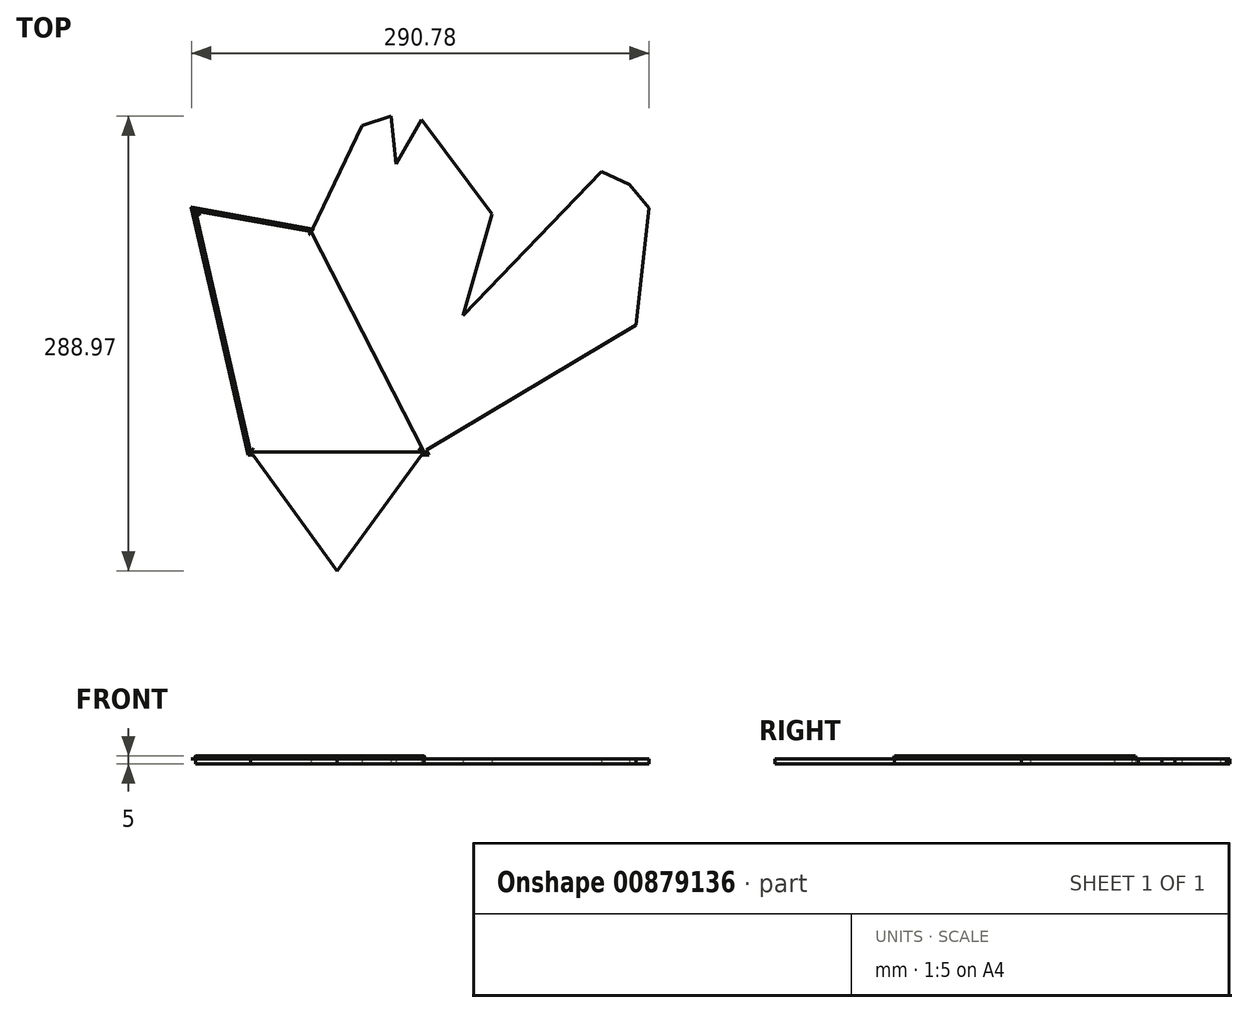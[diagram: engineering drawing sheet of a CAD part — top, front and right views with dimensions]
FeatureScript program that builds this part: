
annotation { "Feature Type Name" : "Feature", "Feature Type Description" : "" }
export const myFeature = defineFeature(function(context is Context, id is Id, definition is map)
    precondition{}
    {
        {
            var Q0;
            Q0=qCreatedBy(makeId("Top.planeOp"),FACE);
            var sketch = newSketch(context, id + "F0", { "sketchPlane" : qUnion([Q0])});
            skLineSegment(sketch, "E0", {"start": v(-120.67, -109.95) * mm, "end": v(-10.67, -109.95) * mm});
            skLineSegment(sketch, "E1", {"start": v(-120.67, -109.95) * mm, "end": v(-140.78, -22.23) * mm});
            skLineSegment(sketch, "E2", {"start": v(-140.78, -22.23) * mm, "end": v(-10.67, -109.95) * mm});
            skLineSegment(sketch, "E3", {"start": v(-10.67, -109.95) * mm, "end": v(-51.68, -29.84) * mm});
            skLineSegment(sketch, "E4", {"start": v(-51.68, -29.84) * mm, "end": v(-140.78, -22.23) * mm});
            skLineSegment(sketch, "E5", {"start": v(-140.78, -22.23) * mm, "end": v(-155.75, 43.08) * mm});
            skLineSegment(sketch, "E6", {"start": v(-155.75, 43.08) * mm, "end": v(-51.68, -29.84) * mm});
            skLineSegment(sketch, "E7", {"start": v(-51.68, -29.84) * mm, "end": v(-82.21, 29.8) * mm});
            skLineSegment(sketch, "E8", {"start": v(-82.21, 29.8) * mm, "end": v(-155.75, 43.08) * mm});
            skLineSegment(sketch, "E9.4.1", {"start": v(-10.67, -109.95) * mm, "end": v(66.55, -63.72) * mm});
            skLineSegment(sketch, "E9.4.7", {"start": v(66.55, -63.72) * mm, "end": v(124.03, -29.3) * mm});
            skPoint(sketch, "E9.center", {"position": v(-65.67, -185.66) * mm});
            skLineSegment(sketch, "E10", {"start": v(-51.68, -29.84) * mm, "end": v(-23.12, 17.9) * mm});
            skLineSegment(sketch, "E11", {"start": v(-82.21, 29.8) * mm, "end": v(-50, 97.22) * mm});
            skLineSegment(sketch, "E12.MirrorCS", {"start": v(-28.45, 72.7) * mm, "end": v(-50, 97.22) * mm});
            skLineSegment(sketch, "E13", {"start": v(-28.45, 72.7) * mm, "end": v(-31.43, 103.3) * mm});
            skLineSegment(sketch, "E14", {"start": v(-31.43, 103.3) * mm, "end": v(-50, 97.22) * mm});
            skLineSegment(sketch, "E15", {"start": v(-28.45, 72.7) * mm, "end": v(-10.67, -109.95) * mm});
            skLineSegment(sketch, "E16.MirrorCS", {"start": v(-31.43, 103.3) * mm, "end": v(-12.04, 100.91) * mm});
            skLineSegment(sketch, "E17.MirrorCS", {"start": v(-28.45, 72.7) * mm, "end": v(-12.04, 100.91) * mm});
            skLineSegment(sketch, "E18.MirrorCS", {"start": v(32.58, 40.97) * mm, "end": v(-12.04, 100.91) * mm});
            skLineSegment(sketch, "E19.MirrorCS", {"start": v(14.12, -23.44) * mm, "end": v(32.58, 40.97) * mm});
            skLineSegment(sketch, "E20.MirrorCS", {"start": v(14.12, -23.44) * mm, "end": v(-23.12, 17.9) * mm});
            skLineSegment(sketch, "E21.MirrorCS", {"start": v(-10.67, -109.95) * mm, "end": v(14.12, -23.44) * mm});
            skLineSegment(sketch, "E22.MirrorCS", {"start": v(119.89, 59.95) * mm, "end": v(132.41, 44.95) * mm});
            skLineSegment(sketch, "E23.MirrorCS", {"start": v(119.89, 59.95) * mm, "end": v(102.17, 68.19) * mm});
            skLineSegment(sketch, "E24.MirrorCS", {"start": v(101.15, 35.56) * mm, "end": v(119.89, 59.95) * mm});
            skLineSegment(sketch, "E25.MirrorCS", {"start": v(101.15, 35.56) * mm, "end": v(102.17, 68.19) * mm});
            skLineSegment(sketch, "E26.MirrorCS", {"start": v(101.15, 35.56) * mm, "end": v(132.41, 44.95) * mm});
            skLineSegment(sketch, "E27.MirrorCS", {"start": v(66.55, -63.72) * mm, "end": v(67.6, -8.1) * mm});
            skLineSegment(sketch, "E28.MirrorCS", {"start": v(32.58, 40.97) * mm, "end": v(102.17, 68.19) * mm});
            skLineSegment(sketch, "E29.MirrorCS", {"start": v(14.12, -23.44) * mm, "end": v(67.6, -8.1) * mm});
            skLineSegment(sketch, "E30.MirrorCS", {"start": v(101.15, 35.56) * mm, "end": v(-10.67, -109.95) * mm});
            skLineSegment(sketch, "E31.MirrorCS", {"start": v(124.03, -29.3) * mm, "end": v(132.41, 44.95) * mm});
            skLineSegment(sketch, "E32", {"start": v(-51.68, -29.84) * mm, "end": v(-50, 97.22) * mm});
            skLineSegment(sketch, "E33", {"start": v(-51.68, -29.84) * mm, "end": v(-28.45, 72.7) * mm});
            skLineSegment(sketch, "E34", {"start": v(-28.45, 72.7) * mm, "end": v(14.12, -23.44) * mm});
            skLineSegment(sketch, "E35", {"start": v(14.12, -23.44) * mm, "end": v(-12.04, 100.91) * mm});
            skLineSegment(sketch, "E36", {"start": v(14.12, -23.44) * mm, "end": v(102.17, 68.19) * mm});
            skLineSegment(sketch, "E37", {"start": v(14.12, -23.44) * mm, "end": v(101.15, 35.56) * mm});
            skLineSegment(sketch, "E38", {"start": v(66.55, -63.72) * mm, "end": v(101.15, 35.56) * mm});
            skLineSegment(sketch, "E39", {"start": v(66.55, -63.72) * mm, "end": v(132.41, 44.95) * mm});
            skLineSegment(sketch, "E40", {"start": v(-65.67, -185.66) * mm, "end": v(-120.67, -109.95) * mm});
            skLineSegment(sketch, "E41", {"start": v(-65.67, -185.66) * mm, "end": v(-10.67, -109.95) * mm});
            skSolve(sketch);
        }
        {
            var Q0;
            Q0 = qSketchRegion(id + "F75ZbTaoLFMl4lC_0", true);
            var Q1;
            {var subQ0=sQuery(id+"F0.wireOp",EDGE,"E10");Q1=makeQuery(id+"F0.imprint","IMPRINT",FACE,{"disambiguationData":[TD([[makeQuery(id+"F0.imprint","IMPRINT",EDGE,{"derivedFrom":subQ0}),1.0]])]});}
            var Q2;
            Q2=makeQuery(id+"F0.imprint","IMPRINT",FACE,{"disambiguationData":[TD([[makeQuery(id+"F0.imprint","IMPRINT",EDGE,{"derivedFrom":sQuery(id+"F0.wireOp",EDGE,"E2")}),1.0]])]});
            var Q3;
            {var subQ0=sQuery(id+"F0.wireOp",EDGE,"E3");Q3=makeQuery(id+"F0.imprint","IMPRINT",FACE,{"disambiguationData":[TD([[makeQuery(id+"F0.imprint","IMPRINT",EDGE,{"derivedFrom":subQ0}),-1.0]])]});}
            var Q4;
            Q4=makeQuery(id+"F0.imprint","IMPRINT",FACE,{"disambiguationData":[TD([[makeQuery(id+"F0.imprint","IMPRINT",EDGE,{"derivedFrom":sQuery(id+"F0.wireOp",EDGE,"E0")}),-1.0]])]});
            var Q5;
            Q5=makeQuery(id+"F0.imprint","IMPRINT",FACE,{"disambiguationData":[TD([[makeQuery(id+"F0.imprint","IMPRINT",EDGE,{"derivedFrom":sQuery(id+"F0.wireOp",EDGE,"E9.4.7")}),1.0]])]});
            var Q6;
            Q6=makeQuery(id+"F0.imprint","IMPRINT",FACE,{"disambiguationData":[TD([[makeQuery(id+"F0.imprint","IMPRINT",EDGE,{"derivedFrom":sQuery(id+"F0.wireOp",EDGE,"E1")}),-1.0]])]});
            var Q7;
            Q7=makeQuery(id+"F0.imprint","IMPRINT",FACE,{"disambiguationData":[TD([[makeQuery(id+"F0.imprint","IMPRINT",EDGE,{"derivedFrom":sQuery(id+"F0.wireOp",EDGE,"E4")}),-1.0]])]});
            var Q8;
            Q8=makeQuery(id+"F0.imprint","IMPRINT",FACE,{"disambiguationData":[TD([[makeQuery(id+"F0.imprint","IMPRINT",EDGE,{"derivedFrom":sQuery(id+"F0.wireOp",EDGE,"E6")}),1.0]])]});
            var Q9;
            Q9=makeQuery(id+"F0.imprint","IMPRINT",FACE,{"disambiguationData":[TD([[makeQuery(id+"F0.imprint","IMPRINT",EDGE,{"derivedFrom":sQuery(id+"F0.wireOp",EDGE,"E7")}),-1.0]])]});
            var Q10;
            {var subQ0=sQuery(id+"F0.wireOp",EDGE,"E9.4.1");Q10=makeQuery(id+"F0.imprint","IMPRINT",FACE,{"disambiguationData":[TD([[makeQuery(id+"F0.imprint","IMPRINT",EDGE,{"derivedFrom":subQ0}),1.0]])]});}
            var Q11;
            Q11=makeQuery(id+"F0.imprint","IMPRINT",FACE,{"disambiguationData":[TD([[makeQuery(id+"F0.imprint","IMPRINT",EDGE,{"derivedFrom":sQuery(id+"F0.wireOp",EDGE,"E12.MirrorCS")}),-1.0]])]});
            var Q12;
            Q12=makeQuery(id+"F0.imprint","IMPRINT",FACE,{"disambiguationData":[TD([[makeQuery(id+"F0.imprint","IMPRINT",EDGE,{"derivedFrom":sQuery(id+"F0.wireOp",EDGE,"E13")}),-1.0]])]});
            var Q13;
            Q13=makeQuery(id+"F0.imprint","IMPRINT",FACE,{"disambiguationData":[TD([[makeQuery(id+"F0.imprint","IMPRINT",EDGE,{"derivedFrom":sQuery(id+"F0.wireOp",EDGE,"E18.MirrorCS")}),1.0]])]});
            var Q14;
            Q14=makeQuery(id+"F0.imprint","IMPRINT",FACE,{"disambiguationData":[TD([[makeQuery(id+"F0.imprint","IMPRINT",EDGE,{"derivedFrom":sQuery(id+"F0.wireOp",EDGE,"E22.MirrorCS")}),-1.0]])]});
            var Q15;
            Q15=makeQuery(id+"F0.imprint","IMPRINT",FACE,{"disambiguationData":[TD([[makeQuery(id+"F0.imprint","IMPRINT",EDGE,{"derivedFrom":sQuery(id+"F0.wireOp",EDGE,"E23.MirrorCS")}),1.0]])]});
            var Q16;
            Q16=makeQuery(id+"F0.imprint","IMPRINT",FACE,{"disambiguationData":[TD([[makeQuery(id+"F0.imprint","IMPRINT",EDGE,{"derivedFrom":sQuery(id+"F0.wireOp",EDGE,"E19.MirrorCS")}),-1.0]])]});
            var Q17;
            Q17=makeQuery(id+"F0.imprint","IMPRINT",FACE,{"disambiguationData":[TD([[makeQuery(id+"F0.imprint","IMPRINT",EDGE,{"derivedFrom":sQuery(id+"F0.wireOp",EDGE,"E12.MirrorCS")}),1.0]])]});
            var Q18;
            {var subQ0=sQuery(id+"F0.wireOp",EDGE,"E20.MirrorCS");Q18=makeQuery(id+"F0.imprint","IMPRINT",FACE,{"disambiguationData":[TD([[makeQuery(id+"F0.imprint","IMPRINT",EDGE,{"derivedFrom":subQ0}),-1.0]])]});}
            var Q19;
            {var subQ2=sQuery(id+"F0.wireOp",EDGE,"E20.MirrorCS");Q19=makeQuery(id+"F0.imprint","IMPRINT",FACE,{"disambiguationData":[TD([[makeQuery(id+"F0.imprint","IMPRINT",EDGE,{"derivedFrom":subQ2}),1.0]])]});}
            var Q20;
            Q20=makeQuery(id+"F0.imprint","IMPRINT",FACE,{"disambiguationData":[TD([[makeQuery(id+"F0.imprint","IMPRINT",EDGE,{"derivedFrom":sQuery(id+"F0.wireOp",EDGE,"E17.MirrorCS")}),-1.0]])]});
            var Q21;
            {var subQ0=sQuery(id+"F0.wireOp",EDGE,"E21.MirrorCS");Q21=makeQuery(id+"F0.imprint","IMPRINT",FACE,{"disambiguationData":[TD([[makeQuery(id+"F0.imprint","IMPRINT",EDGE,{"derivedFrom":subQ0}),-1.0]])]});}
            var Q22;
            Q22=makeQuery(id+"F0.imprint","IMPRINT",FACE,{"disambiguationData":[TD([[makeQuery(id+"F0.imprint","IMPRINT",EDGE,{"derivedFrom":sQuery(id+"F0.wireOp",EDGE,"E25.MirrorCS")}),1.0]])]});
            var Q23;
            Q23=makeQuery(id+"F0.imprint","IMPRINT",FACE,{"disambiguationData":[TD([[makeQuery(id+"F0.imprint","IMPRINT",EDGE,{"derivedFrom":sQuery(id+"F0.wireOp",EDGE,"E26.MirrorCS")}),-1.0]])]});
            var Q24;
            {var subQ0=sQuery(id+"F0.wireOp",EDGE,"E27.MirrorCS");Q24=makeQuery(id+"F0.imprint","IMPRINT",FACE,{"disambiguationData":[TD([[makeQuery(id+"F0.imprint","IMPRINT",EDGE,{"derivedFrom":subQ0}),-1.0]])]});}
            var Q25;
            {var subQ0=sQuery(id+"F0.wireOp",EDGE,"E29.MirrorCS");Q25=makeQuery(id+"F0.imprint","IMPRINT",FACE,{"disambiguationData":[TD([[makeQuery(id+"F0.imprint","IMPRINT",EDGE,{"derivedFrom":subQ0}),1.0]])]});}
            extrude(context, id + "F1", {"entities" : qUnion([Q0, Q1, Q2, Q3, Q4, Q5, Q6, Q7, Q8, Q9, Q10, Q11, Q12, Q13, Q14, Q15, Q16, Q17, Q18, Q19, Q20, Q21, Q22, Q23, Q24, Q25]), "depth" : 3 * mm, "offsetDistance" : 25 * mm});
        }
        {
            var Q0;
            Q0=makeQuery(id+"F1.opExtrude","CAP_FACE",FACE,{"disambiguationData":[OSD([sQuery(id+"F0.wireOp",EDGE,"E1"),sQuery(id+"F0.wireOp",EDGE,"E5"),sQuery(id+"F0.wireOp",EDGE,"E8"),sQuery(id+"F0.wireOp",EDGE,"E9.4.1"),sQuery(id+"F0.wireOp",EDGE,"E9.4.7"),sQuery(id+"F0.wireOp",EDGE,"E11"),sQuery(id+"F0.wireOp",EDGE,"E14"),sQuery(id+"F0.wireOp",EDGE,"E16.MirrorCS"),sQuery(id+"F0.wireOp",EDGE,"E18.MirrorCS"),sQuery(id+"F0.wireOp",EDGE,"E22.MirrorCS"),sQuery(id+"F0.wireOp",EDGE,"E23.MirrorCS"),sQuery(id+"F0.wireOp",EDGE,"E28.MirrorCS"),sQuery(id+"F0.wireOp",EDGE,"E31.MirrorCS"),sQuery(id+"F0.wireOp",EDGE,"E40"),sQuery(id+"F0.wireOp",EDGE,"E41")])],"isStart":false});
            var sketch = newSketch(context, id + "F2", { "sketchPlane" : qUnion([Q0])});
            skLineSegment(sketch, "E42", {"start": v(-120.67, -109.95) * mm, "end": v(-10.67, -109.95) * mm});
            skLineSegment(sketch, "E43", {"start": v(-120.67, -109.95) * mm, "end": v(-140.78, -22.23) * mm});
            skLineSegment(sketch, "E44", {"start": v(-140.78, -22.23) * mm, "end": v(-10.67, -109.95) * mm});
            skLineSegment(sketch, "E45", {"start": v(-10.67, -109.95) * mm, "end": v(-51.68, -29.84) * mm});
            skLineSegment(sketch, "E46", {"start": v(-51.68, -29.84) * mm, "end": v(-140.78, -22.23) * mm});
            skLineSegment(sketch, "E47", {"start": v(-140.78, -22.23) * mm, "end": v(-155.75, 43.08) * mm});
            skLineSegment(sketch, "E48", {"start": v(-155.75, 43.08) * mm, "end": v(-51.68, -29.84) * mm});
            skLineSegment(sketch, "E49", {"start": v(-51.68, -29.84) * mm, "end": v(-82.21, 29.8) * mm});
            skLineSegment(sketch, "E50", {"start": v(-82.21, 29.8) * mm, "end": v(-155.75, 43.08) * mm});
            skLineSegment(sketch, "E51.4.1", {"start": v(-10.67, -109.95) * mm, "end": v(66.55, -63.72) * mm});
            skLineSegment(sketch, "E51.4.7", {"start": v(66.55, -63.72) * mm, "end": v(124.03, -29.3) * mm});
            skPoint(sketch, "E51.center", {"position": v(-65.67, -185.66) * mm});
            skLineSegment(sketch, "E52", {"start": v(-51.68, -29.84) * mm, "end": v(-23.12, 17.9) * mm});
            skLineSegment(sketch, "E53", {"start": v(-82.21, 29.8) * mm, "end": v(-50, 97.22) * mm});
            skLineSegment(sketch, "E54.MirrorCS", {"start": v(-28.45, 72.7) * mm, "end": v(-50, 97.22) * mm});
            skLineSegment(sketch, "E55", {"start": v(-28.45, 72.7) * mm, "end": v(-31.43, 103.3) * mm});
            skLineSegment(sketch, "E56", {"start": v(-31.43, 103.3) * mm, "end": v(-50, 97.22) * mm});
            skLineSegment(sketch, "E57", {"start": v(-28.45, 72.7) * mm, "end": v(-10.67, -109.95) * mm});
            skLineSegment(sketch, "E58.MirrorCS", {"start": v(-31.43, 103.3) * mm, "end": v(-12.04, 100.91) * mm});
            skLineSegment(sketch, "E59.MirrorCS", {"start": v(-28.45, 72.7) * mm, "end": v(-12.04, 100.91) * mm});
            skLineSegment(sketch, "E60.MirrorCS", {"start": v(32.58, 40.97) * mm, "end": v(-12.04, 100.91) * mm});
            skLineSegment(sketch, "E61.MirrorCS", {"start": v(14.12, -23.44) * mm, "end": v(32.58, 40.97) * mm});
            skLineSegment(sketch, "E62.MirrorCS", {"start": v(14.12, -23.44) * mm, "end": v(-23.12, 17.9) * mm});
            skLineSegment(sketch, "E63.MirrorCS", {"start": v(-10.67, -109.95) * mm, "end": v(14.12, -23.44) * mm});
            skLineSegment(sketch, "E64.MirrorCS", {"start": v(119.89, 59.95) * mm, "end": v(132.41, 44.95) * mm});
            skLineSegment(sketch, "E65.MirrorCS", {"start": v(119.89, 59.95) * mm, "end": v(102.17, 68.19) * mm});
            skLineSegment(sketch, "E66.MirrorCS", {"start": v(101.15, 35.56) * mm, "end": v(119.89, 59.95) * mm});
            skLineSegment(sketch, "E67.MirrorCS", {"start": v(101.15, 35.56) * mm, "end": v(102.17, 68.19) * mm});
            skLineSegment(sketch, "E68.MirrorCS", {"start": v(101.15, 35.56) * mm, "end": v(132.41, 44.95) * mm});
            skLineSegment(sketch, "E69.MirrorCS", {"start": v(66.55, -63.72) * mm, "end": v(67.6, -8.1) * mm});
            skLineSegment(sketch, "E70.MirrorCS", {"start": v(32.58, 40.97) * mm, "end": v(102.17, 68.19) * mm});
            skLineSegment(sketch, "E71.MirrorCS", {"start": v(14.12, -23.44) * mm, "end": v(67.6, -8.1) * mm});
            skLineSegment(sketch, "E72.MirrorCS", {"start": v(101.15, 35.56) * mm, "end": v(-10.67, -109.95) * mm});
            skLineSegment(sketch, "E73.MirrorCS", {"start": v(124.03, -29.3) * mm, "end": v(132.41, 44.95) * mm});
            skLineSegment(sketch, "E74", {"start": v(-51.68, -29.84) * mm, "end": v(-50, 97.22) * mm});
            skLineSegment(sketch, "E75", {"start": v(-51.68, -29.84) * mm, "end": v(-28.45, 72.7) * mm});
            skLineSegment(sketch, "E76", {"start": v(-28.45, 72.7) * mm, "end": v(14.12, -23.44) * mm});
            skLineSegment(sketch, "E77", {"start": v(14.12, -23.44) * mm, "end": v(-12.04, 100.91) * mm});
            skLineSegment(sketch, "E78", {"start": v(14.12, -23.44) * mm, "end": v(102.17, 68.19) * mm});
            skLineSegment(sketch, "E79", {"start": v(14.12, -23.44) * mm, "end": v(101.15, 35.56) * mm});
            skLineSegment(sketch, "E80", {"start": v(66.55, -63.72) * mm, "end": v(101.15, 35.56) * mm});
            skLineSegment(sketch, "E81", {"start": v(66.55, -63.72) * mm, "end": v(132.41, 44.95) * mm});
            skLineSegment(sketch, "E82", {"start": v(-65.67, -185.66) * mm, "end": v(-120.67, -109.95) * mm});
            skLineSegment(sketch, "E83", {"start": v(-65.67, -185.66) * mm, "end": v(-10.67, -109.95) * mm});
            skSolve(sketch);
        }
        {
            var Q0;
            Q0=qCreatedBy(makeId("Right.planeOp"),FACE);
            var sketch = newSketch(context, id + "F3", { "sketchPlane" : qUnion([Q0])});
            skLineSegment(sketch, "E84.bottom", {"start": v(-13.38, 35.38) * mm, "end": v(-66.44, 35.38) * mm});
            skLineSegment(sketch, "E84.top", {"start": v(-13.38, 7.26) * mm, "end": v(-66.44, 7.26) * mm});
            skLineSegment(sketch, "E84.left", {"start": v(-13.38, 35.38) * mm, "end": v(-13.38, 7.26) * mm});
            skLineSegment(sketch, "E84.right", {"start": v(-66.44, 35.38) * mm, "end": v(-66.44, 7.26) * mm});
            skSolve(sketch);
        }
        {
            var Q0;
            Q0=makeQuery(id+"F3.imprint","IMPRINT",FACE,{"disambiguationData":[TD([[makeQuery(id+"F3.imprint","IMPRINT",EDGE,{"derivedFrom":sQuery(id+"F3.wireOp",EDGE,"E84.bottom")}),1.0]])]});
            var Q1;
            Q1=sQuery(id+"F2.wireOp",VERTEX,"E42.start");
            cPlane(context, id + "F4", {"entities" : qUnion([Q0, Q1]), "cplaneType" : CPlaneType.PLANE_POINT, "offset" : 25 * mm, "width" : 150 * mm, "height" : 150 * mm});
        }
        {
            var Q0;
            Q0=qCreatedBy(id+"F4.planeOp",FACE);
            var sketch = newSketch(context, id + "F5", { "sketchPlane" : qUnion([Q0])});
            skLineSegment(sketch, "E85", {"start": v(-107.95, 3) * mm, "end": v(-111.95, 3) * mm});
            skPoint(sketch, "E86.endSnap0", {"position": v(-109.95, 3) * mm});
            skFitSpline(sketch, "E87", {"points": [v(-111.95, 3) * mm, v(-110.34, 4.08) * mm], "startDerivative": vector(2.23, 0) * mm, "endDerivative": vector(1.31, 3.17) * mm});
            skLineSegment(sketch, "E88", {"start": v(-109.95, 3) * mm, "end": v(-109.95, 5) * mm, "construction": true});
            skLineSegment(sketch, "E89", {"start": v(-110.34, 4.08) * mm, "end": v(-109.95, 5) * mm});
            skLineSegment(sketch, "E90.MirrorCS", {"start": v(-109.57, 4.08) * mm, "end": v(-109.95, 5) * mm});
            skFitSpline(sketch, "E91.MirrorCS", {"points": [v(-107.95, 3) * mm, v(-109.57, 4.08) * mm], "startDerivative": vector(-2.23, 0) * mm, "endDerivative": vector(-1.31, 3.17) * mm});
            skFitSpline(sketch, "E92.MirrorCS", {"points": [v(-107.95, 3) * mm, v(-109.57, 4.08) * mm], "startDerivative": vector(-2.23, 0) * mm, "endDerivative": vector(-1.31, 3.17) * mm});
            skSolve(sketch);
        }
        {
            var Q0;
            Q0=makeQuery(id+"F5.imprint","IMPRINT",FACE,{"disambiguationData":[TD([[makeQuery(id+"F5.imprint","IMPRINT",EDGE,{"derivedFrom":sQuery(id+"F5.wireOp",EDGE,"E85")}),-1.0]])]});
            var Q1;
            Q1=sQuery(id+"F2.wireOp",EDGE,"E45");
            var Q2;
            Q2=sQuery(id+"F2.wireOp",EDGE,"E49");
            var Q3;
            Q3=sQuery(id+"F2.wireOp",EDGE,"E42");
            var Q4;
            Q4=sQuery(id+"F2.wireOp",EDGE,"E50");
            var Q5;
            Q5=sQuery(id+"F2.wireOp",EDGE,"E47");
            var Q6;
            Q6=sQuery(id+"F2.wireOp",EDGE,"E43");
            sweep(context, id + "F6", {"operationType" : NewBodyOperationType.ADD, "profiles" : qUnion([Q0]), "path" : qUnion([Q1, Q2, Q3, Q4, Q5, Q6])});
        }
    });
